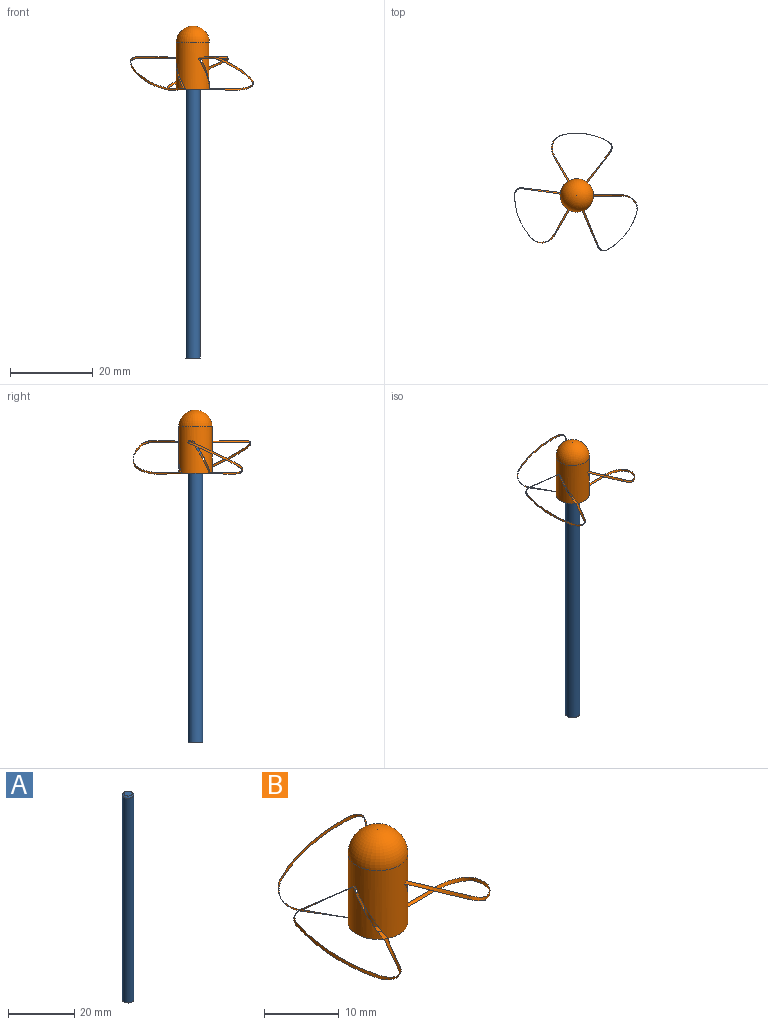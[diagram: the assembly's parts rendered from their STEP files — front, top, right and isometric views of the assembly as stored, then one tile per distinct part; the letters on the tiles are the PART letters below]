
ASSEMBLY  parts=2 mates=1
PART A: 4 faces, bbox 3.8x3.8x76.2 mm
  f0: cylinder r=1.75mm len=75.69mm, axis (0,0,-1), area 832.3mm2, adj f2,f3
  f1: plane 2.48x2.48mm, normal (0,0,1), area 4.8mm2, adj f3
  f2: plane 3.5x3.5mm, normal (0,0,-1), area 9.6mm2, adj f0
  f3: torus R=1.24mm, axis (0,0,1), area 7.8mm2, adj f0,f1
PART B: 26 faces, bbox 30.5x29x16.2 mm
  f0: cylinder r=4mm len=11.25mm, axis (0,0,-1), area 269.2mm2, adj f2,f6,f9,f11,f17,f18,f21,f23
  f1: plane 0.02x0.02mm, normal (0,0,1), area 0mm2, adj f6
  f2: plane 8.05x8.04mm, normal (0,0,-1), area 34.3mm2, adj f0,f7,f8,f19,f20
  f3: cylinder r=1.75mm len=10.41mm, axis (0,0,-1), area 114.5mm2, adj f5,f7
  f4: plane 2.48x2.48mm, normal (0,0,-1), area 4.8mm2, adj f5
  f5: torus R=1.24mm, axis (0,0,-1), area 7.8mm2, adj f3,f4
  f6: torus R=0.01mm, axis (0,0,1), area 100.4mm2, adj f0,f1
  f7: cone r=1.75mm half-angle=45deg, axis (0,0,-1), area 9mm2, adj f2,f3
  f8: bspline ~2.5x1.77mm, area 0mm2, adj f2,f9
  f9: bspline ~7.02x0.44mm, area 3.5mm2, adj f0,f8,f12
  f10: bspline ~9.18x7.26mm, area 6.5mm2, adj f12,f13
  f11: bspline ~10.39x4.54mm, area 4.7mm2, adj f0,f13
  f12: bspline ~4.77x4.7mm, area 3.4mm2, adj f9,f10
  f13: bspline ~2.5x1.86mm, area 1.5mm2, adj f10,f11
  f14: bspline ~5.72x4.12mm, area 3.4mm2, adj f15,f18
  f15: bspline ~10.88x5.56mm, area 6.5mm2, adj f14,f16
  f16: bspline ~1.98x1.93mm, area 1.5mm2, adj f15,f17
  f17: bspline ~11.06x1.77mm, area 4.7mm2, adj f0,f16
  f18: bspline ~9.68x5.77mm, area 3.5mm2, adj f0,f14,f19
  f19: bspline ~2.5x1.38mm, area 0mm2, adj f2,f18
  f20: bspline ~2.5x1.69mm, area 0mm2, adj f2,f21
  f21: bspline ~6.24x3.8mm, area 3.5mm2, adj f0,f20,f24
  f22: bspline ~11.59x5.56mm, area 6.5mm2, adj f24,f25
  f23: bspline ~9.01x7.02mm, area 4.7mm2, adj f0,f25
  f24: bspline ~5.15x4.35mm, area 3.4mm2, adj f21,f22
  f25: bspline ~2.54x1.69mm, area 1.5mm2, adj f22,f23
PLACE A t=(12.08,2,-48.9)mm
PLACE B t=(12.08,2,-22.23)mm
MATE cylindrical B.f3 <-> A.f0  axis (0,0,-1) through (12.08,2,-10.8)mm
